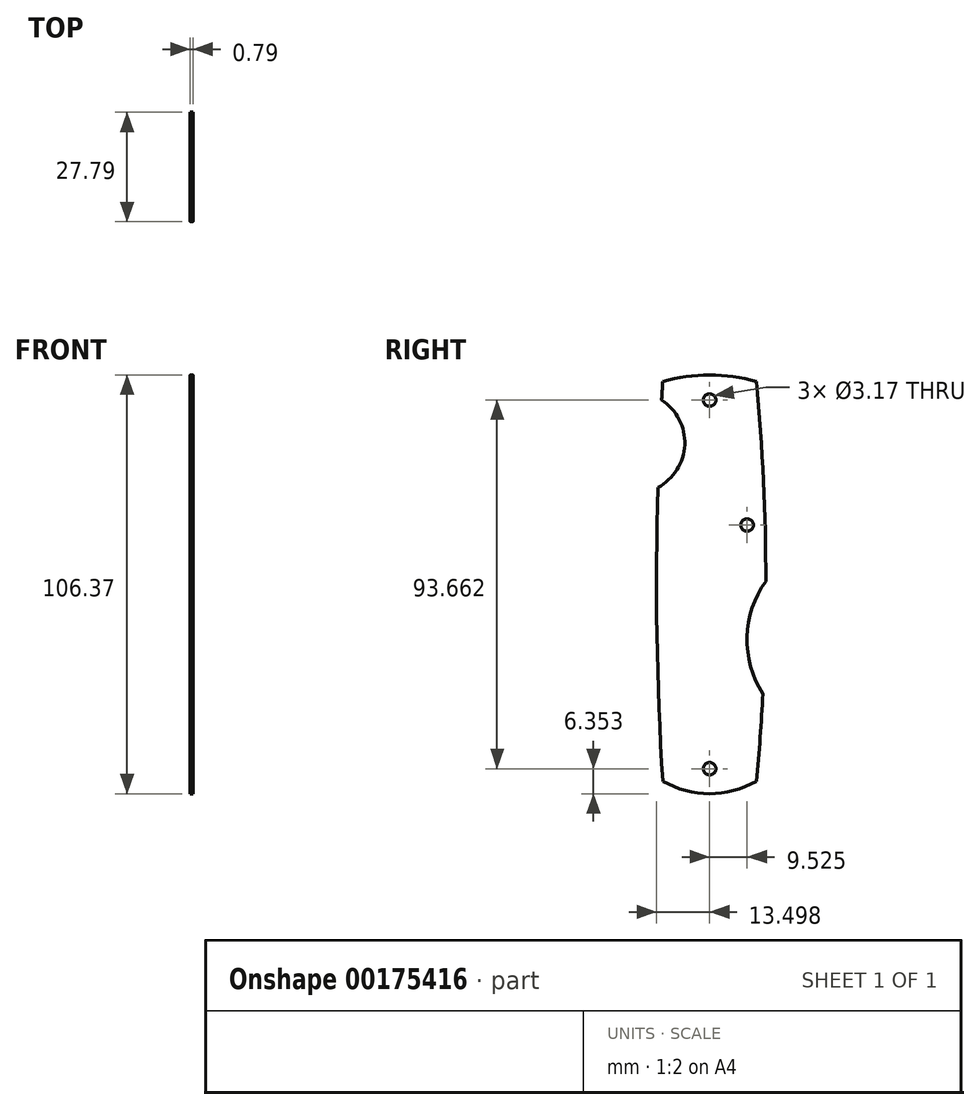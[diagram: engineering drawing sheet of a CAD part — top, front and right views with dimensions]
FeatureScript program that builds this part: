
annotation { "Feature Type Name" : "Feature", "Feature Type Description" : "" }
export const myFeature = defineFeature(function(context is Context, id is Id, definition is map)
    precondition{}
    {
        {
            var Q0;
            Q0=qCreatedBy(makeId("Right.planeOp"),FACE);
            var sketch = newSketch(context, id + "F0", { "sketchPlane" : qUnion([Q0])});
            skLineSegment(sketch, "E0", {"start": v(-2.7, 46.8) * mm, "end": v(-2.7, -54.8) * mm, "construction": true});
            skPoint(sketch, "E1", {"position": v(-2.7, 42.05) * mm});
            skCircle(sketch, "E2", {"center": v(-2.7, 42.05) * mm, "radius": 1.59 * mm});
            skLineSegment(sketch, "E3", {"start": v(-12.22, 42.05) * mm, "end": v(6.83, 42.05) * mm, "construction": true});
            skLineSegment(sketch, "E4", {"start": v(6.83, 42.05) * mm, "end": v(6.83, -21.45) * mm, "construction": true});
            skPoint(sketch, "E5", {"position": v(6.83, 10.3) * mm});
            skCircle(sketch, "E6", {"center": v(6.83, 10.3) * mm, "radius": 1.59 * mm});
            skLineSegment(sketch, "E7", {"start": v(-14.6, 46.8) * mm, "end": v(9.21, 46.8) * mm, "construction": true});
            skPoint(sketch, "E8", {"position": v(-2.7, 10.3) * mm});
            skLineSegment(sketch, "E9", {"start": v(-2.7, 10.3) * mm, "end": v(10, 10.3) * mm, "construction": true});
            skPoint(sketch, "E10", {"position": v(6.83, -4) * mm});
            skLineSegment(sketch, "E11", {"start": v(6.83, -4) * mm, "end": v(11.6, -4) * mm, "construction": true});
            skLineSegment(sketch, "E12.MirrorCS", {"start": v(-2.7, -18.28) * mm, "end": v(10, -18.28) * mm, "construction": true});
            skPoint(sketch, "E13.MirrorP", {"position": v(6.83, -18.28) * mm});
            skLineSegment(sketch, "E14", {"start": v(9.21, -54.8) * mm, "end": v(-14.6, -54.8) * mm, "construction": true});
            skArc(sketch, "E15", {"start": v(9.21, -54.8) * mm, "mid": v(11.6, -4) * mm, "end": v(9.21, 46.8) * mm});
            skLineSegment(sketch, "E16.MirrorCS", {"start": v(6.83, -32.57) * mm, "end": v(11.6, -32.57) * mm, "construction": true});
            skPoint(sketch, "E17", {"position": v(10.84, -32.57) * mm});
            skArc(sketch, "E18", {"start": v(11.6, -4) * mm, "mid": v(6.84, -18.16) * mm, "end": v(10.84, -32.57) * mm});
            skLineSegment(sketch, "E19", {"start": v(-2.7, -54.8) * mm, "end": v(-2.7, -57.97) * mm, "construction": true});
            skArc(sketch, "E20", {"start": v(-14.6, -54.8) * mm, "mid": v(-2.7, -57.97) * mm, "end": v(9.21, -54.8) * mm});
            skLineSegment(sketch, "E21", {"start": v(-2.7, 46.8) * mm, "end": v(-2.7, 48.4) * mm, "construction": true});
            skArc(sketch, "E22", {"start": v(9.21, 46.8) * mm, "mid": v(-2.7, 48.4) * mm, "end": v(-14.6, 46.8) * mm});
            skLineSegment(sketch, "E23", {"start": v(-14.6, 46.8) * mm, "end": v(-14.6, -54.8) * mm, "construction": true});
            skLineSegment(sketch, "E24", {"start": v(-14.6, -4) * mm, "end": v(-16.19, -4) * mm, "construction": true});
            skPoint(sketch, "E24.endSnap0", {"position": v(-14.6, -4) * mm});
            skArc(sketch, "E25", {"start": v(-14.6, 46.8) * mm, "mid": v(-16.19, -4) * mm, "end": v(-14.6, -54.8) * mm});
            skPoint(sketch, "E26", {"position": v(-2.7, -51.62) * mm});
            skCircle(sketch, "E27", {"center": v(-2.7, -51.62) * mm, "radius": 1.59 * mm});
            skPoint(sketch, "E28", {"position": v(-14.88, 42.05) * mm});
            skPoint(sketch, "E29", {"position": v(-15.84, 19.84) * mm});
            skLineSegment(sketch, "E30", {"start": v(-15.38, 32.12) * mm, "end": v(-9.03, 32.12) * mm, "construction": true});
            skArc(sketch, "E31", {"start": v(-15.84, 19.84) * mm, "mid": v(-9.02, 30.67) * mm, "end": v(-14.88, 42.05) * mm});
            skSolve(sketch);
        }
        {
            var Q0;
            Q0=makeQuery(id+"F0.imprint","IMPRINT",FACE,{"disambiguationData":[TD([[makeQuery(id+"F0.imprint","IMPRINT",EDGE,{"derivedFrom":sQuery(id+"F0.wireOp",EDGE,"E2")}),-1.0]])]});
            extrude(context, id + "F1", {"entities" : qUnion([Q0]), "depth" : 0.8 * mm});
        }
    });
